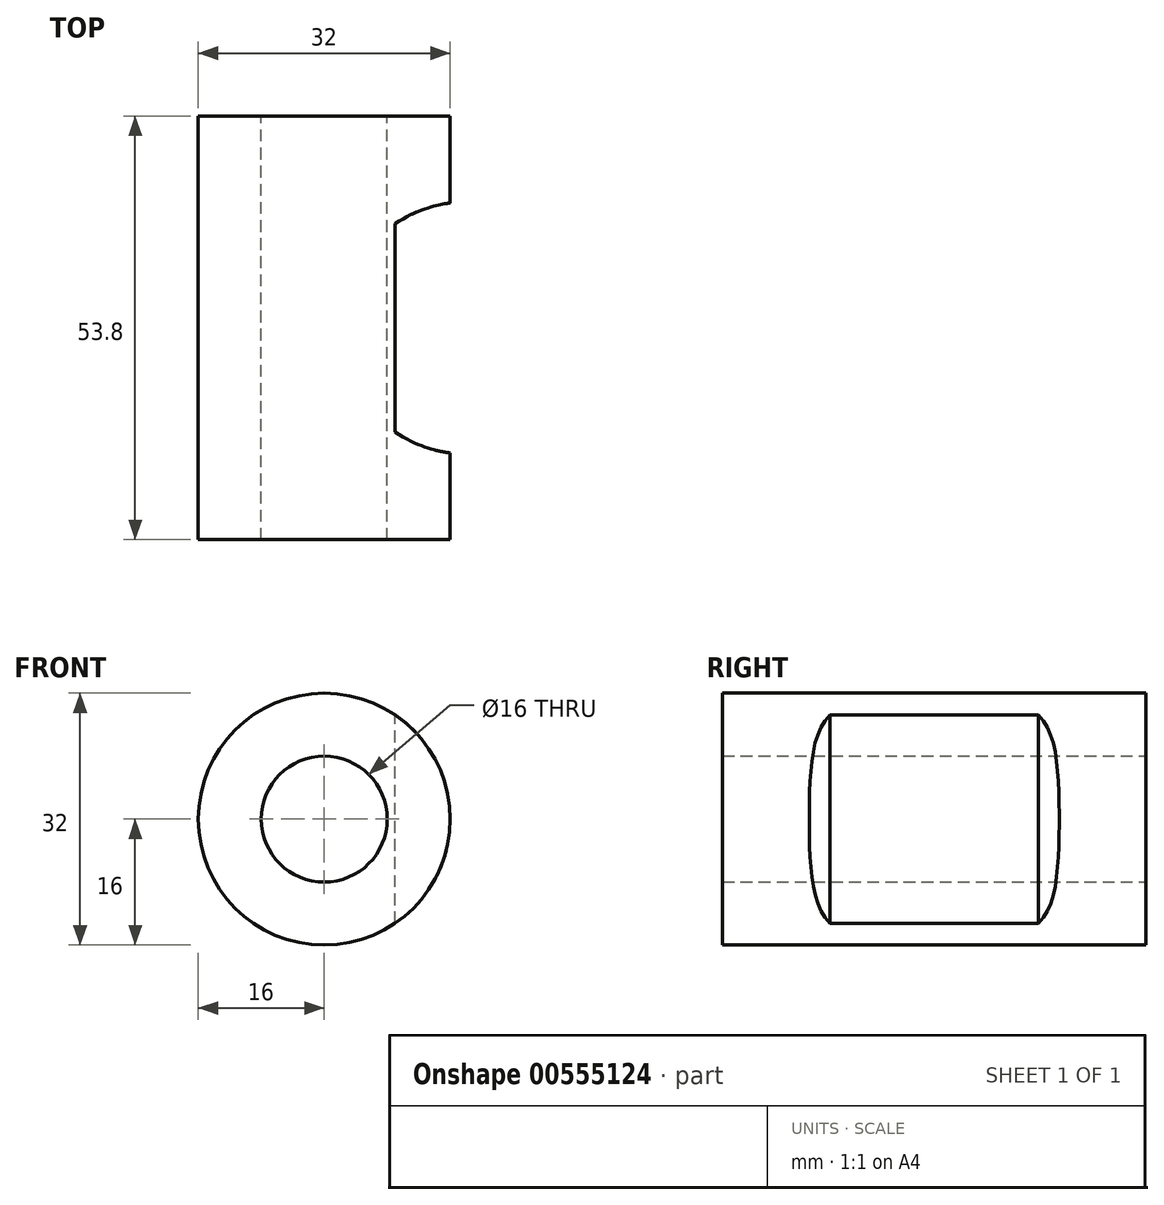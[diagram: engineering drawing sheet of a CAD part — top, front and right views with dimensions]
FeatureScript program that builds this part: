
annotation { "Feature Type Name" : "Feature", "Feature Type Description" : "" }
export const myFeature = defineFeature(function(context is Context, id is Id, definition is map)
    precondition{}
    {
        {
            var Q0;
            Q0=qCreatedBy(makeId("Front.planeOp"),FACE);
            var sketch = newSketch(context, id + "F0", { "sketchPlane" : qUnion([Q0])});
            skCircle(sketch, "E0", {"center": v(0, 0) * mm, "radius": 8 * mm});
            skCircle(sketch, "E1", {"center": v(0, 0) * mm, "radius": 16 * mm});
            skSolve(sketch);
        }
        {
            var Q0;
            Q0=makeQuery(id+"F0.imprint","IMPRINT",FACE,{"disambiguationData":[TD([[makeQuery(id+"F0.imprint","IMPRINT",EDGE,{"derivedFrom":sQuery(id+"F0.wireOp",EDGE,"E0")}),-1.0]])]});
            extrude(context, id + "F1", {"entities" : qUnion([Q0]), "depth" : 53.8 * mm, "offsetDistance" : 25 * mm});
        }
        {
            var Q0;
            Q0=qCreatedBy(makeId("Top.planeOp"),FACE);
            var sketch = newSketch(context, id + "F2", { "sketchPlane" : qUnion([Q0])});
            skArc(sketch, "E2", {"start": v(9, -40.13) * mm, "mid": v(34, -26.9) * mm, "end": v(9, -13.67) * mm});
            skLineSegment(sketch, "E3", {"start": v(9, -40.13) * mm, "end": v(9, -13.67) * mm});
            skPoint(sketch, "E4.orphan", {"position": v(18, -53.8) * mm});
            skPoint(sketch, "E5.end.orphan", {"position": v(18, 0) * mm});
            skSolve(sketch);
        }
        {
            var Q0;
            Q0=makeQuery(id+"F2.imprint","IMPRINT",FACE,{"disambiguationData":[TD([[makeQuery(id+"F2.imprint","IMPRINT",EDGE,{"derivedFrom":sQuery(id+"F2.wireOp",EDGE,"E2")}),1.0]])]});
            extrude(context, id + "F3", {"entities" : qUnion([Q0]), "operationType" : NewBodyOperationType.REMOVE, "oppositeDirection" : true, "depth" : 25 * mm, "offsetDistance" : 25 * mm, "hasSecondDirection" : true, "secondDirectionBound" : BoundingType.THROUGH_ALL, "secondDirectionOppositeDirection" : false, "secondDirectionDepth" : 25 * mm});
        }
    });
